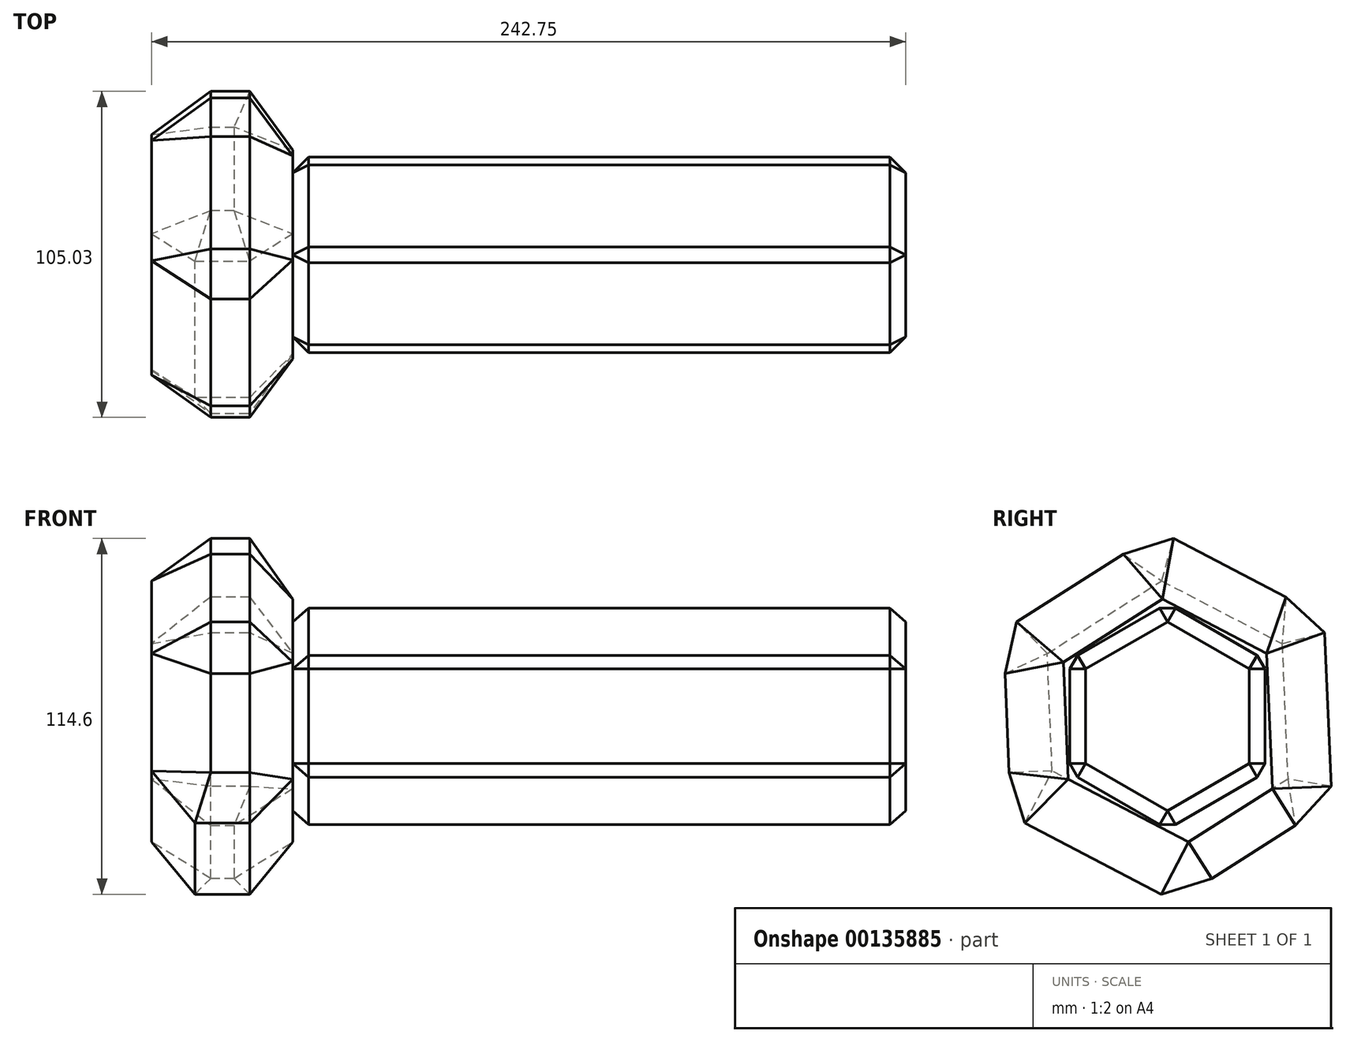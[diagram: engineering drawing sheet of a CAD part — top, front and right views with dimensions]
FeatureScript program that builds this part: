
annotation { "Feature Type Name" : "Feature", "Feature Type Description" : "" }
export const myFeature = defineFeature(function(context is Context, id is Id, definition is map)
    precondition{}
    {
        {
            var Q0;
            Q0=qCreatedBy(makeId("Front.planeOp"),FACE);
            var sketch = newSketch(context, id + "F0", { "sketchPlane" : qUnion([Q0])});
            skLineSegment(sketch, "E0", {"start": v(58.94, -65.33) * mm, "end": v(51.4, -65.33) * mm});
            skLineSegment(sketch, "E1", {"start": v(51.4, -65.33) * mm, "end": v(58.94, -65.33) * mm});
            skLineSegment(sketch, "E2", {"start": v(0, 0) * mm, "end": v(197.31, 0) * mm});
            skSolve(sketch);
        }
        {
            var Q0;
            Q0=qCreatedBy(makeId("Right.planeOp"),FACE);
            var sketch = newSketch(context, id + "F1", { "sketchPlane" : qUnion([Q0])});
            skCircle(sketch, "E3.cCircle", {"center": v(0, 0) * mm, "radius": 31.46 * mm, "construction": true});
            skLineSegment(sketch, "E3.0", {"start": v(31.46, 18.17) * mm, "end": v(31.46, -18.17) * mm});
            skLineSegment(sketch, "E3.1", {"start": v(31.46, -18.17) * mm, "end": v(0, -36.33) * mm});
            skLineSegment(sketch, "E3.2", {"start": v(0, -36.33) * mm, "end": v(-31.46, -18.17) * mm});
            skLineSegment(sketch, "E3.3", {"start": v(-31.46, -18.17) * mm, "end": v(-31.46, 18.17) * mm});
            skLineSegment(sketch, "E3.4", {"start": v(-31.46, 18.17) * mm, "end": v(0, 36.33) * mm});
            skLineSegment(sketch, "E3.5", {"start": v(0, 36.33) * mm, "end": v(31.46, 18.17) * mm});
            skPoint(sketch, "E3.0.midPoint", {"position": v(31.46, 0) * mm});
            skSolve(sketch);
        }
        {
            var Q0;
            Q0=makeQuery(id+"F1.imprint","IMPRINT",FACE,{"disambiguationData":[TD([[makeQuery(id+"F1.imprint","IMPRINT",EDGE,{"derivedFrom":sQuery(id+"F1.wireOp",EDGE,"E3.0")}),-1.0]])]});
            var Q1;
            Q1=sQuery(id+"F0.wireOp",EDGE,"E2");
            sweep(context, id + "F2", {"profiles" : qUnion([Q0]), "path" : qUnion([Q1])});
        }
        {
            var Q0;
            Q0=makeQuery(id+"F2.opSweep","SWEPT_EDGE",EDGE,{"disambiguationData":[OSD([sQuery(id+"F0.wireOp",EDGE,"E2"),sQuery(id+"F1.wireOp",EDGE,"E3.4"),sQuery(id+"F1.wireOp",EDGE,"E3.5")])]});
            var Q1;
            Q1=makeQuery(id+"F2.opSweep","CAP_EDGE",EDGE,{"disambiguationData":[OSD([sQuery(id+"F0.wireOp",VERTEX,"E2.end"),sQuery(id+"F1.wireOp",EDGE,"E3.5")])],"isStart":false});
            var Q2;
            Q2=makeQuery(id+"F2.opSweep","SWEPT_EDGE",EDGE,{"disambiguationData":[OSD([sQuery(id+"F0.wireOp",EDGE,"E2"),sQuery(id+"F1.wireOp",EDGE,"E3.2"),sQuery(id+"F1.wireOp",EDGE,"E3.3")])]});
            var Q3;
            Q3=makeQuery(id+"F2.opSweep","CAP_EDGE",EDGE,{"disambiguationData":[OSD([sQuery(id+"F0.wireOp",VERTEX,"E2.start"),sQuery(id+"F1.wireOp",EDGE,"E3.0")])],"isStart":true});
            var Q4;
            Q4=makeQuery(id+"F2.opSweep","SWEPT_EDGE",EDGE,{"disambiguationData":[OSD([sQuery(id+"F0.wireOp",EDGE,"E2"),sQuery(id+"F1.wireOp",EDGE,"E3.0"),sQuery(id+"F1.wireOp",EDGE,"E3.5")])]});
            var Q5;
            Q5=makeQuery(id+"F2.opSweep","CAP_EDGE",EDGE,{"disambiguationData":[OSD([sQuery(id+"F0.wireOp",VERTEX,"E2.start"),sQuery(id+"F1.wireOp",EDGE,"E3.5")])],"isStart":true});
            var Q6;
            Q6=makeQuery(id+"F2.opSweep","SWEPT_EDGE",EDGE,{"disambiguationData":[OSD([sQuery(id+"F0.wireOp",EDGE,"E2"),sQuery(id+"F1.wireOp",EDGE,"E3.3"),sQuery(id+"F1.wireOp",EDGE,"E3.4")])]});
            var Q7;
            Q7=makeQuery(id+"F2.opSweep","CAP_EDGE",EDGE,{"disambiguationData":[OSD([sQuery(id+"F0.wireOp",VERTEX,"E2.end"),sQuery(id+"F1.wireOp",EDGE,"E3.4")])],"isStart":false});
            var Q8;
            Q8=makeQuery(id+"F2.opSweep","CAP_EDGE",EDGE,{"disambiguationData":[OSD([sQuery(id+"F0.wireOp",VERTEX,"E2.start"),sQuery(id+"F1.wireOp",EDGE,"E3.3")])],"isStart":true});
            var Q9;
            Q9=makeQuery(id+"F2.opSweep","SWEPT_EDGE",EDGE,{"disambiguationData":[OSD([sQuery(id+"F0.wireOp",EDGE,"E2"),sQuery(id+"F1.wireOp",EDGE,"E3.1"),sQuery(id+"F1.wireOp",EDGE,"E3.2")])]});
            var Q10;
            Q10=makeQuery(id+"F2.opSweep","CAP_EDGE",EDGE,{"disambiguationData":[OSD([sQuery(id+"F0.wireOp",VERTEX,"E2.start"),sQuery(id+"F1.wireOp",EDGE,"E3.4")])],"isStart":true});
            var Q11;
            Q11=makeQuery(id+"F2.opSweep","CAP_EDGE",EDGE,{"disambiguationData":[OSD([sQuery(id+"F0.wireOp",VERTEX,"E2.end"),sQuery(id+"F1.wireOp",EDGE,"E3.2")])],"isStart":false});
            var Q12;
            Q12=makeQuery(id+"F2.opSweep","CAP_EDGE",EDGE,{"disambiguationData":[OSD([sQuery(id+"F0.wireOp",VERTEX,"E2.end"),sQuery(id+"F1.wireOp",EDGE,"E3.1")])],"isStart":false});
            var Q13;
            Q13=makeQuery(id+"F2.opSweep","CAP_EDGE",EDGE,{"disambiguationData":[OSD([sQuery(id+"F0.wireOp",VERTEX,"E2.start"),sQuery(id+"F1.wireOp",EDGE,"E3.2")])],"isStart":true});
            var Q14;
            Q14=makeQuery(id+"F2.opSweep","SWEPT_EDGE",EDGE,{"disambiguationData":[OSD([sQuery(id+"F0.wireOp",EDGE,"E2"),sQuery(id+"F1.wireOp",EDGE,"E3.0"),sQuery(id+"F1.wireOp",EDGE,"E3.1")])]});
            var Q15;
            Q15=makeQuery(id+"F2.opSweep","CAP_EDGE",EDGE,{"disambiguationData":[OSD([sQuery(id+"F0.wireOp",VERTEX,"E2.start"),sQuery(id+"F1.wireOp",EDGE,"E3.1")])],"isStart":true});
            var Q16;
            Q16=makeQuery(id+"F2.opSweep","CAP_EDGE",EDGE,{"disambiguationData":[OSD([sQuery(id+"F0.wireOp",VERTEX,"E2.end"),sQuery(id+"F1.wireOp",EDGE,"E3.0")])],"isStart":false});
            var Q17;
            Q17=makeQuery(id+"F2.opSweep","CAP_EDGE",EDGE,{"disambiguationData":[OSD([sQuery(id+"F0.wireOp",VERTEX,"E2.end"),sQuery(id+"F1.wireOp",EDGE,"E3.3")])],"isStart":false});
            chamfer(context, id + "F3", {"entities" : qUnion([Q0, Q1, Q2, Q3, Q4, Q5, Q6, Q7, Q8, Q9, Q10, Q11, Q12, Q13, Q14, Q15, Q16, Q17]), "width" : 5.08 * mm, "tangentPropagation" : true});
        }
        {
            var Q0;
            Q0=qCreatedBy(makeId("Right.planeOp"),FACE);
            var sketch = newSketch(context, id + "F4", { "sketchPlane" : qUnion([Q0])});
            skCircle(sketch, "E4.cCircle", {"center": v(0, 0) * mm, "radius": 51.7 * mm, "construction": true});
            skLineSegment(sketch, "E4.0", {"start": v(52.92, -27.64) * mm, "end": v(2.52, -59.65) * mm});
            skLineSegment(sketch, "E4.1", {"start": v(2.52, -59.65) * mm, "end": v(-50.4, -32) * mm});
            skLineSegment(sketch, "E4.2", {"start": v(-50.4, -32) * mm, "end": v(-52.92, 27.64) * mm});
            skLineSegment(sketch, "E4.3", {"start": v(-52.92, 27.64) * mm, "end": v(-2.52, 59.65) * mm});
            skLineSegment(sketch, "E4.4", {"start": v(-2.52, 59.65) * mm, "end": v(50.4, 32) * mm});
            skLineSegment(sketch, "E4.5", {"start": v(50.4, 32) * mm, "end": v(52.92, -27.64) * mm});
            skPoint(sketch, "E4.0.midPoint", {"position": v(27.72, -43.65) * mm});
            skSolve(sketch);
        }
        {
            var Q0;
            Q0=makeQuery(id+"F4.imprint","IMPRINT",FACE,{"disambiguationData":[TD([[makeQuery(id+"F4.imprint","IMPRINT",EDGE,{"derivedFrom":sQuery(id+"F4.wireOp",EDGE,"E4.0")}),-1.0]])]});
            extrude(context, id + "F5", {"entities" : qUnion([Q0]), "operationType" : NewBodyOperationType.ADD, "oppositeDirection" : true, "depth" : 45.44 * mm});
        }
        {
            var Q0;
            Q0=makeQuery(id+"F5.opExtrude","SWEPT_EDGE",EDGE,{"disambiguationData":[OSD([sQuery(id+"F4.wireOp",EDGE,"E4.0"),sQuery(id+"F4.wireOp",EDGE,"E4.1")])]});
            var Q1;
            Q1=makeQuery(id+"F5.opExtrude","CAP_EDGE",EDGE,{"disambiguationData":[OSD([sQuery(id+"F4.wireOp",EDGE,"E4.2")])],"isStart":false});
            var Q2;
            Q2=makeQuery(id+"F5.opExtrude","CAP_EDGE",EDGE,{"disambiguationData":[OSD([sQuery(id+"F4.wireOp",EDGE,"E4.3")])],"isStart":false});
            var Q3;
            Q3=makeQuery(id+"F5.opExtrude","CAP_EDGE",EDGE,{"disambiguationData":[OSD([sQuery(id+"F4.wireOp",EDGE,"E4.1")])],"isStart":true});
            var Q4;
            Q4=makeQuery(id+"F5.opExtrude","CAP_EDGE",EDGE,{"disambiguationData":[OSD([sQuery(id+"F4.wireOp",EDGE,"E4.5")])],"isStart":false});
            var Q5;
            Q5=makeQuery(id+"F5.opExtrude","SWEPT_EDGE",EDGE,{"disambiguationData":[OSD([sQuery(id+"F4.wireOp",EDGE,"E4.4"),sQuery(id+"F4.wireOp",EDGE,"E4.5")])]});
            var Q6;
            Q6=makeQuery(id+"F5.opExtrude","CAP_EDGE",EDGE,{"disambiguationData":[OSD([sQuery(id+"F4.wireOp",EDGE,"E4.5")])],"isStart":true});
            var Q7;
            Q7=makeQuery(id+"F5.opExtrude","CAP_EDGE",EDGE,{"disambiguationData":[OSD([sQuery(id+"F4.wireOp",EDGE,"E4.1")])],"isStart":false});
            var Q8;
            Q8=makeQuery(id+"F5.opExtrude","SWEPT_EDGE",EDGE,{"disambiguationData":[OSD([sQuery(id+"F4.wireOp",EDGE,"E4.0"),sQuery(id+"F4.wireOp",EDGE,"E4.5")])]});
            var Q9;
            Q9=makeQuery(id+"F5.opExtrude","SWEPT_EDGE",EDGE,{"disambiguationData":[OSD([sQuery(id+"F4.wireOp",EDGE,"E4.1"),sQuery(id+"F4.wireOp",EDGE,"E4.2")])]});
            var Q10;
            Q10=makeQuery(id+"F5.opExtrude","CAP_EDGE",EDGE,{"disambiguationData":[OSD([sQuery(id+"F4.wireOp",EDGE,"E4.3")])],"isStart":true});
            var Q11;
            Q11=makeQuery(id+"F5.opExtrude","CAP_EDGE",EDGE,{"disambiguationData":[OSD([sQuery(id+"F4.wireOp",EDGE,"E4.0")])],"isStart":false});
            var Q12;
            Q12=makeQuery(id+"F5.opExtrude","CAP_EDGE",EDGE,{"disambiguationData":[OSD([sQuery(id+"F4.wireOp",EDGE,"E4.4")])],"isStart":false});
            var Q13;
            Q13=makeQuery(id+"F5.opExtrude","SWEPT_EDGE",EDGE,{"disambiguationData":[OSD([sQuery(id+"F4.wireOp",EDGE,"E4.2"),sQuery(id+"F4.wireOp",EDGE,"E4.3")])]});
            var Q14;
            Q14=makeQuery(id+"F5.opExtrude","CAP_EDGE",EDGE,{"disambiguationData":[OSD([sQuery(id+"F4.wireOp",EDGE,"E4.2")])],"isStart":true});
            var Q15;
            Q15=makeQuery(id+"F5.opExtrude","SWEPT_EDGE",EDGE,{"disambiguationData":[OSD([sQuery(id+"F4.wireOp",EDGE,"E4.3"),sQuery(id+"F4.wireOp",EDGE,"E4.4")])]});
            var Q16;
            Q16=makeQuery(id+"F5.opExtrude","CAP_EDGE",EDGE,{"disambiguationData":[OSD([sQuery(id+"F4.wireOp",EDGE,"E4.4")])],"isStart":true});
            var Q17;
            Q17=makeQuery(id+"F5.opExtrude","CAP_EDGE",EDGE,{"disambiguationData":[OSD([sQuery(id+"F4.wireOp",EDGE,"E4.0")])],"isStart":true});
            chamfer(context, id + "F6", {"entities" : qUnion([Q0, Q1, Q2, Q3, Q4, Q5, Q6, Q7, Q8, Q9, Q10, Q11, Q12, Q13, Q14, Q15, Q16, Q17]), "chamferType" : ChamferType.OFFSET_ANGLE, "width" : 5.08 * mm, "oppositeDirection" : false, "angle" : 45 * degree, "tangentPropagation" : true});
        }
    });
